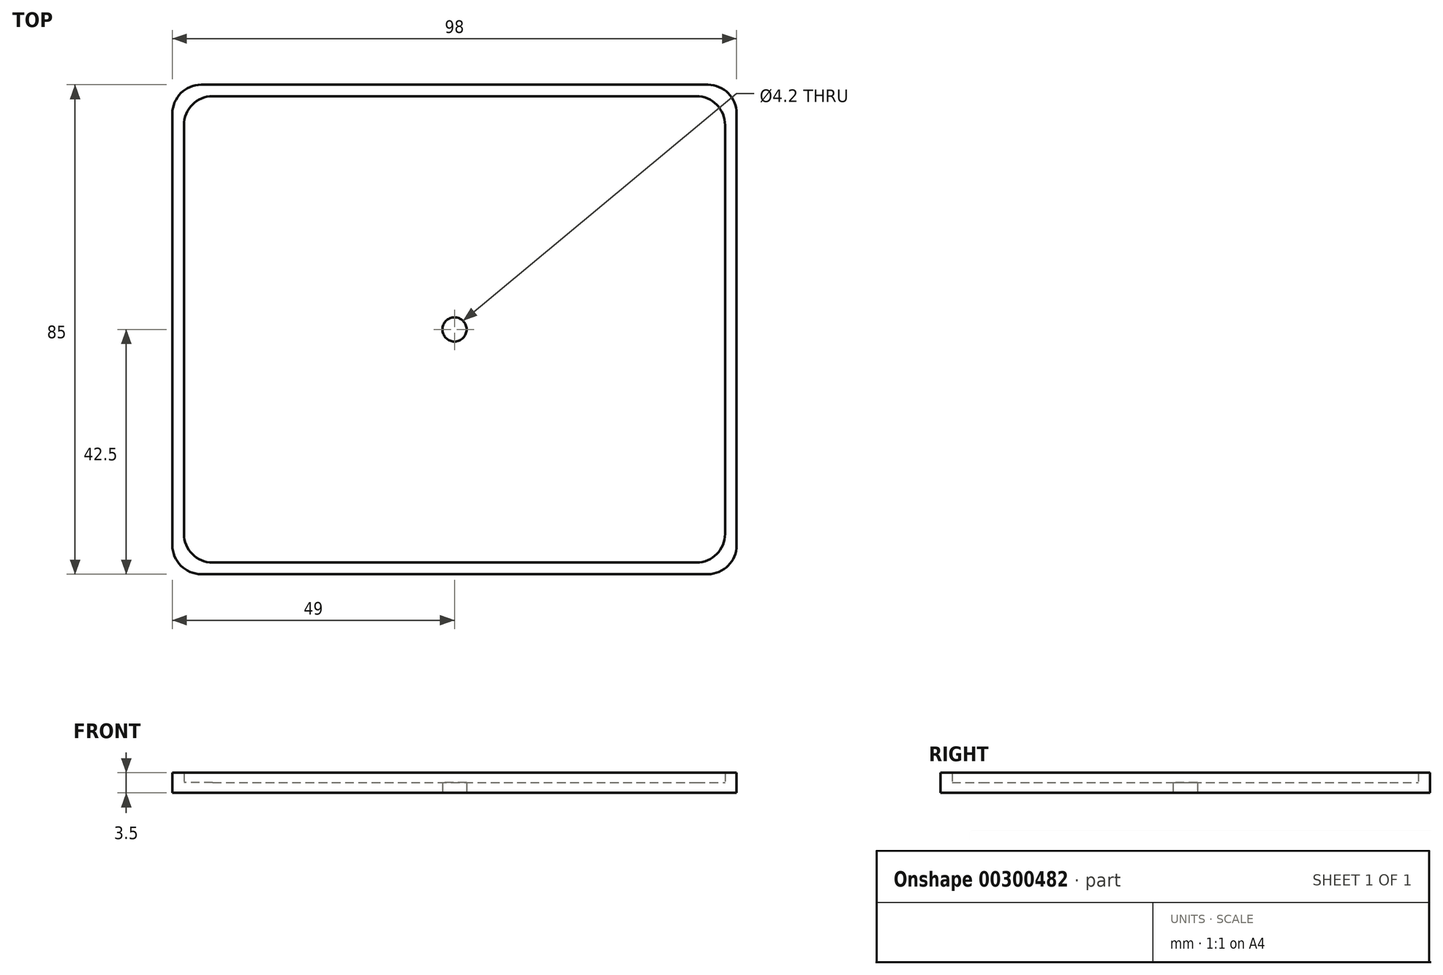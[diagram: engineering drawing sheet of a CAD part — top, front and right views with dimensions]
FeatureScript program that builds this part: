
annotation { "Feature Type Name" : "Feature", "Feature Type Description" : "" }
export const myFeature = defineFeature(function(context is Context, id is Id, definition is map)
    precondition{}
    {
        {
            var Q0;
            Q0=qCreatedBy(makeId("Top.planeOp"),FACE);
            var sketch = newSketch(context, id + "F0", { "sketchPlane" : qUnion([Q0])});
            skLineSegment(sketch, "E0", {"start": v(0, 0) * mm, "end": v(-98, 0) * mm});
            skLineSegment(sketch, "E1", {"start": v(-98, 0) * mm, "end": v(-98, 85) * mm});
            skLineSegment(sketch, "E2", {"start": v(-98, 85) * mm, "end": v(0, 85) * mm});
            skLineSegment(sketch, "E3", {"start": v(0, 85) * mm, "end": v(0, 0) * mm});
            skLineSegment(sketch, "E4", {"start": v(-49, 85) * mm, "end": v(-49, 42.5) * mm});
            skPoint(sketch, "E4.endSnap0", {"position": v(-98, 42.5) * mm});
            skCircle(sketch, "E5", {"center": v(-49, 42.5) * mm, "radius": 2.1 * mm});
            skLineSegment(sketch, "E6.0", {"start": v(-96, 83) * mm, "end": v(-2, 83) * mm});
            skLineSegment(sketch, "E6.1", {"start": v(-96, 2) * mm, "end": v(-96, 83) * mm});
            skLineSegment(sketch, "E6.2", {"start": v(-2, 2) * mm, "end": v(-96, 2) * mm});
            skLineSegment(sketch, "E6.3", {"start": v(-2, 83) * mm, "end": v(-2, 2) * mm});
            skSolve(sketch);
        }
        {
            var Q0;
            Q0 = qSketchRegion(id + "F0", true);
            var Q1;
            Q1=makeQuery(id+"F0.imprint","IMPRINT",FACE,{"disambiguationData":[TD([[makeQuery(id+"F0.imprint","IMPRINT",EDGE,{"derivedFrom":sQuery(id+"F0.wireOp",EDGE,"E0")}),-1.0]])]});
            var Q2;
            Q2=makeQuery(id+"F0.imprint","IMPRINT",FACE,{"disambiguationData":[TD([[makeQuery(id+"F0.imprint","IMPRINT",EDGE,{"derivedFrom":sQuery(id+"F0.wireOp",EDGE,"ffe3b29c-6f3a-40e6-b081-ee23909a9d80.sketch_text.stroke-0")}),-1.0]])]});
            var Q3;
            Q3=makeQuery(id+"F0.imprint","IMPRINT",FACE,{"disambiguationData":[TD([[makeQuery(id+"F0.imprint","IMPRINT",EDGE,{"derivedFrom":sQuery(id+"F0.wireOp",EDGE,"ffe3b29c-6f3a-40e6-b081-ee23909a9d80.sketch_text.stroke-19")}),-1.0]])]});
            var Q4;
            Q4=makeQuery(id+"F0.imprint","IMPRINT",FACE,{"disambiguationData":[TD([[makeQuery(id+"F0.imprint","IMPRINT",EDGE,{"derivedFrom":sQuery(id+"F0.wireOp",EDGE,"E5")}),-1.0]])]});
            extrude(context, id + "F1", {"entities" : qUnion([Q0, Q1, Q2, Q3, Q4]), "depth" : 1.8 * mm, "offsetDistance" : 25 * mm});
        }
        {
            var Q0;
            Q0=makeQuery(id+"F1.opExtrude","SWEPT_EDGE",EDGE,{"disambiguationData":[OSD([sQuery(id+"F0.wireOp",EDGE,"E1"),sQuery(id+"F0.wireOp",EDGE,"E2")])]});
            var Q1;
            Q1=makeQuery(id+"F1.opExtrude","SWEPT_EDGE",EDGE,{"disambiguationData":[OSD([sQuery(id+"F0.wireOp",EDGE,"E0"),sQuery(id+"F0.wireOp",EDGE,"E1")])]});
            var Q2;
            Q2=makeQuery(id+"F1.opExtrude","SWEPT_EDGE",EDGE,{"disambiguationData":[OSD([sQuery(id+"F0.wireOp",EDGE,"E0"),sQuery(id+"F0.wireOp",EDGE,"E3")])]});
            var Q3;
            Q3=makeQuery(id+"F1.opExtrude","SWEPT_EDGE",EDGE,{"disambiguationData":[OSD([sQuery(id+"F0.wireOp",EDGE,"E2"),sQuery(id+"F0.wireOp",EDGE,"E3")])]});
            fillet(context, id + "F2", {"entities" : qUnion([Q0, Q1, Q2, Q3]), "radius" : 5 * mm, "tangentPropagation" : true, "allowEdgeOverflow" : false});
        }
        {
            var Q0;
            Q0=makeQuery(id+"F0.imprint","IMPRINT",FACE,{"disambiguationData":[TD([[makeQuery(id+"F0.imprint","IMPRINT",EDGE,{"derivedFrom":sQuery(id+"F0.wireOp",EDGE,"ffe3b29c-6f3a-40e6-b081-ee23909a9d80.sketch_text.stroke-19")}),-1.0]])]});
            var Q1;
            Q1=makeQuery(id+"F0.imprint","IMPRINT",FACE,{"disambiguationData":[TD([[makeQuery(id+"F0.imprint","IMPRINT",EDGE,{"derivedFrom":sQuery(id+"F0.wireOp",EDGE,"ffe3b29c-6f3a-40e6-b081-ee23909a9d80.sketch_text.stroke-0")}),-1.0]])]});
            var Q2;
            Q2=makeQuery(id+"F0.imprint","IMPRINT",FACE,{"disambiguationData":[TD([[makeQuery(id+"F0.imprint","IMPRINT",EDGE,{"derivedFrom":sQuery(id+"F0.wireOp",EDGE,"E0")}),-1.0]])]});
            extrude(context, id + "F3", {"entities" : qUnion([Q0, Q1, Q2]), "operationType" : NewBodyOperationType.ADD, "depth" : 3.5 * mm, "offsetDistance" : 25 * mm});
        }
        {
            var Q0;
            Q0=makeQuery(id+"F3.opExtrude","SWEPT_EDGE",EDGE,{"disambiguationData":[OSD([sQuery(id+"F0.wireOp",EDGE,"E2"),sQuery(id+"F0.wireOp",EDGE,"E3")])]});
            var Q1;
            Q1=makeQuery(id+"F3.opExtrude","SWEPT_EDGE",EDGE,{"disambiguationData":[OSD([sQuery(id+"F0.wireOp",EDGE,"E0"),sQuery(id+"F0.wireOp",EDGE,"E3")])]});
            var Q2;
            Q2=makeQuery(id+"F3.opExtrude","SWEPT_EDGE",EDGE,{"disambiguationData":[OSD([sQuery(id+"F0.wireOp",EDGE,"E0"),sQuery(id+"F0.wireOp",EDGE,"E1")])]});
            var Q3;
            Q3=makeQuery(id+"F3.opExtrude","SWEPT_EDGE",EDGE,{"disambiguationData":[OSD([sQuery(id+"F0.wireOp",EDGE,"E1"),sQuery(id+"F0.wireOp",EDGE,"E2")])]});
            fillet(context, id + "F4", {"entities" : qUnion([Q0, Q1, Q2, Q3]), "radius" : 5 * mm, "tangentPropagation" : true, "allowEdgeOverflow" : false});
        }
        {
            var Q0;
            Q0=makeQuery(id+"F3.opExtrude","SWEPT_EDGE",EDGE,{"disambiguationData":[OSD([sQuery(id+"F0.wireOp",EDGE,"E6.0"),sQuery(id+"F0.wireOp",EDGE,"E6.1")])]});
            var Q1;
            Q1=makeQuery(id+"F3.opExtrude","SWEPT_EDGE",EDGE,{"disambiguationData":[OSD([sQuery(id+"F0.wireOp",EDGE,"E6.1"),sQuery(id+"F0.wireOp",EDGE,"E6.2")])]});
            var Q2;
            Q2=makeQuery(id+"F3.opExtrude","SWEPT_EDGE",EDGE,{"disambiguationData":[OSD([sQuery(id+"F0.wireOp",EDGE,"E6.0"),sQuery(id+"F0.wireOp",EDGE,"E6.3")])]});
            var Q3;
            Q3=makeQuery(id+"F3.opExtrude","SWEPT_EDGE",EDGE,{"disambiguationData":[OSD([sQuery(id+"F0.wireOp",EDGE,"E6.2"),sQuery(id+"F0.wireOp",EDGE,"E6.3")])]});
            fillet(context, id + "F5", {"entities" : qUnion([Q0, Q1, Q2, Q3]), "radius" : 5 * mm, "tangentPropagation" : true, "allowEdgeOverflow" : false});
        }
    });
